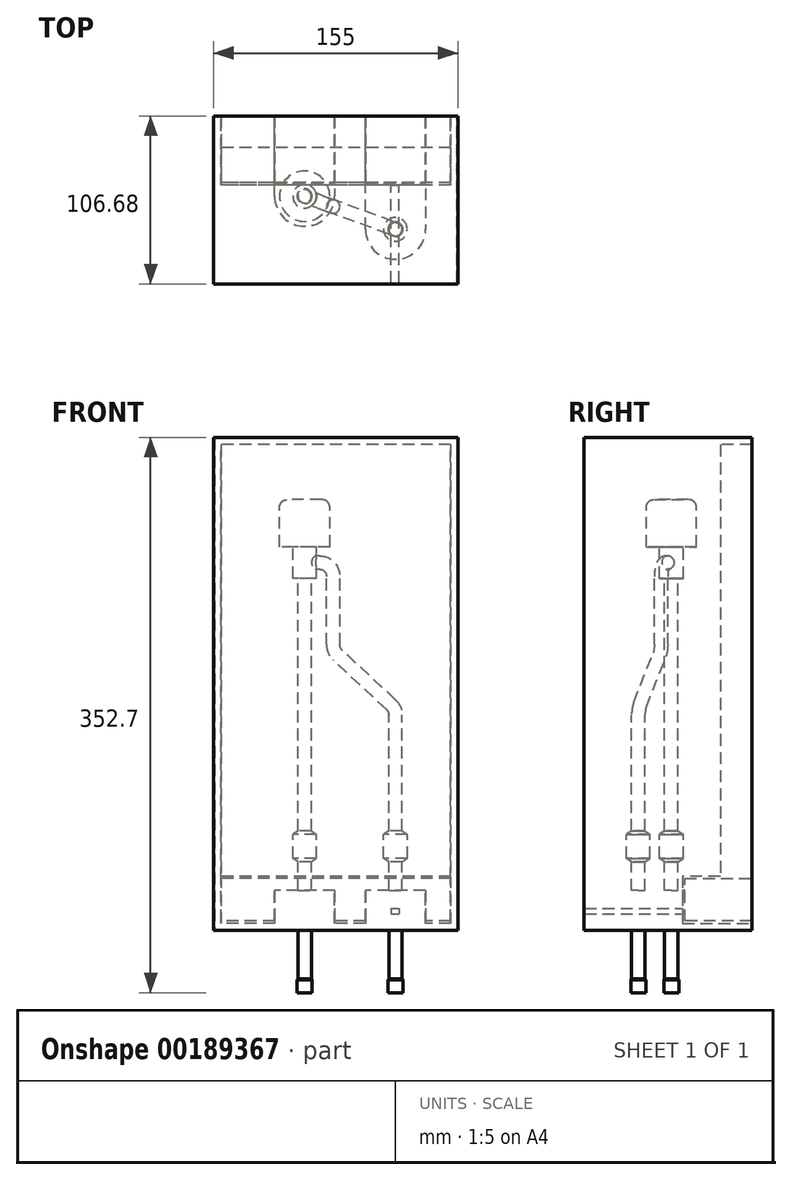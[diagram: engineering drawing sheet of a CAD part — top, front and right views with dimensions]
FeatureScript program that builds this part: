
annotation { "Feature Type Name" : "Feature", "Feature Type Description" : "" }
export const myFeature = defineFeature(function(context is Context, id is Id, definition is map)
    precondition{}
    {
        {
            var Q0;
            Q0=qCreatedBy(makeId("Right.planeOp"),FACE);
            var sketch = newSketch(context, id + "F0", { "sketchPlane" : qUnion([Q0])});
            skLineSegment(sketch, "E0", {"start": v(0, 302.68) * mm, "end": v(-20, 302.68) * mm});
            skLineSegment(sketch, "E1", {"start": v(-20, 302.68) * mm, "end": v(-20, 28.48) * mm});
            skLineSegment(sketch, "E2", {"start": v(-20, 28.48) * mm, "end": v(-44, 28.48) * mm});
            skLineSegment(sketch, "E3", {"start": v(-44, 28.48) * mm, "end": v(-44, -1.52) * mm});
            skLineSegment(sketch, "E4", {"start": v(-44, -1.52) * mm, "end": v(0, -1.52) * mm});
            skLineSegment(sketch, "E5", {"start": v(0, -1.52) * mm, "end": v(0, 0) * mm});
            skLineSegment(sketch, "E6", {"start": v(0, 0) * mm, "end": v(-42.48, 0) * mm});
            skLineSegment(sketch, "E7", {"start": v(-42.48, 0) * mm, "end": v(-42.48, 26.95) * mm});
            skLineSegment(sketch, "E8", {"start": v(-42.48, 26.95) * mm, "end": v(0, 26.95) * mm});
            skLineSegment(sketch, "E9", {"start": v(0, 26.95) * mm, "end": v(0, 302.68) * mm});
            skLineSegment(sketch, "E10", {"start": v(-42.48, 26.95) * mm, "end": v(-42.48, 28.48) * mm, "construction": true});
            skLineSegment(sketch, "E11", {"start": v(-42.48, 26.95) * mm, "end": v(-44, 26.95) * mm, "construction": true});
            skSolve(sketch);
        }
        {
            var Q0;
            Q0 = qSketchRegion(id + "F0", true);
            extrude(context, id + "F1", {"entities" : qUnion([Q0]), "endBound" : BoundingType.SYMMETRIC, "depth" : 146 * mm});
        }
        {
            var Q0;
            Q0=qCreatedBy(makeId("Front.planeOp"),FACE);
            cPlane(context, id + "F2", {"entities" : qUnion([Q0]), "cplaneType" : CPlaneType.OFFSET, "offset" : 51 * mm, "width" : 152.4 * mm, "height" : 152.4 * mm});
        }
        {
            var Q0;
            Q0=qCreatedBy(makeId("Front.planeOp"),FACE);
            cPlane(context, id + "F3", {"entities" : qUnion([Q0]), "cplaneType" : CPlaneType.OFFSET, "offset" : 72 * mm, "width" : 152.4 * mm, "height" : 152.4 * mm});
        }
        {
            var Q0;
            Q0=qCreatedBy(id+"F2.planeOp",FACE);
            var sketch = newSketch(context, id + "F4", { "sketchPlane" : qUnion([Q0])});
            skLineSegment(sketch, "E12", {"start": v(-19.78, 311.1) * mm, "end": v(-19.78, -128.37) * mm, "construction": true});
            skLineSegment(sketch, "E13", {"start": v(-19.78, 267.68) * mm, "end": v(-3.78, 267.68) * mm});
            skLineSegment(sketch, "E14", {"start": v(-3.78, 267.68) * mm, "end": v(-3.78, 237.68) * mm});
            skLineSegment(sketch, "E15", {"start": v(-3.78, 237.68) * mm, "end": v(-12.28, 237.68) * mm});
            skLineSegment(sketch, "E16", {"start": v(-12.28, 237.68) * mm, "end": v(-12.28, 217.68) * mm});
            skLineSegment(sketch, "E17", {"start": v(-12.28, 217.68) * mm, "end": v(-15.53, 217.68) * mm});
            skLineSegment(sketch, "E18", {"start": v(-15.53, 217.68) * mm, "end": v(-15.53, 57.25) * mm});
            skLineSegment(sketch, "E19", {"start": v(-15.53, 57.25) * mm, "end": v(-12.28, 54.92) * mm});
            skLineSegment(sketch, "E20", {"start": v(-12.28, 54.92) * mm, "end": v(-12.28, 39.92) * mm});
            skLineSegment(sketch, "E21", {"start": v(-12.28, 39.92) * mm, "end": v(-15.53, 37.58) * mm});
            skLineSegment(sketch, "E22", {"start": v(-15.53, 37.58) * mm, "end": v(-15.53, -36.66) * mm});
            skLineSegment(sketch, "E23", {"start": v(-15.53, -36.66) * mm, "end": v(-15.02, -37.52) * mm});
            skLineSegment(sketch, "E24", {"start": v(-15.02, -37.52) * mm, "end": v(-15.02, -45.52) * mm});
            skLineSegment(sketch, "E25", {"start": v(-15.02, -45.52) * mm, "end": v(-19.78, -45.52) * mm});
            skLineSegment(sketch, "E26", {"start": v(-19.78, 267.68) * mm, "end": v(-19.78, -45.52) * mm});
            skLineSegment(sketch, "E27", {"start": v(-12.28, 227.68) * mm, "end": v(-19.78, 227.68) * mm, "construction": true});
            skSolve(sketch);
        }
        {
            var Q0;
            Q0 = qSketchRegion(id + "F4", true);
            var Q1;
            Q1=sQuery(id+"F4.wireOp",EDGE,"E12");
            revolve(context, id + "F5", {"entities" : qUnion([Q0]), "axis" : qUnion([Q1]), "revolveType" : RevolveType.FULL});
        }
        {
            var Q0;
            Q0=makeQuery(id+"F5.opRevolve","SWEPT_EDGE",EDGE,{"disambiguationData":[OSD([sQuery(id+"F4.wireOp",EDGE,"E13"),sQuery(id+"F4.wireOp",EDGE,"E14")])]});
            fillet(context, id + "F6", {"entities" : qUnion([Q0]), "radius" : 5.08 * mm, "tangentPropagation" : true, "allowEdgeOverflow" : false});
        }
        {
            var Q0;
            Q0=qCreatedBy(id+"F3.planeOp",FACE);
            var sketch = newSketch(context, id + "F7", { "sketchPlane" : qUnion([Q0])});
            skLineSegment(sketch, "E28", {"start": v(37.92, 349.3) * mm, "end": v(37.92, -165.57) * mm, "construction": true});
            skLineSegment(sketch, "E29", {"start": v(37.92, -45.52) * mm, "end": v(42.68, -45.52) * mm});
            skLineSegment(sketch, "E30", {"start": v(42.68, -45.52) * mm, "end": v(42.68, -37.52) * mm});
            skLineSegment(sketch, "E31", {"start": v(42.68, -37.52) * mm, "end": v(42.17, -36.66) * mm});
            skLineSegment(sketch, "E32", {"start": v(42.17, -36.66) * mm, "end": v(42.17, 37.58) * mm});
            skLineSegment(sketch, "E33", {"start": v(42.17, 37.58) * mm, "end": v(45.42, 39.92) * mm});
            skLineSegment(sketch, "E34", {"start": v(45.42, 39.92) * mm, "end": v(45.42, 54.92) * mm});
            skLineSegment(sketch, "E35", {"start": v(45.42, 54.92) * mm, "end": v(42.17, 57.25) * mm});
            skLineSegment(sketch, "E36", {"start": v(42.17, 57.25) * mm, "end": v(42.17, 124.92) * mm});
            skLineSegment(sketch, "E37", {"start": v(42.17, 124.92) * mm, "end": v(37.92, 124.92) * mm});
            skLineSegment(sketch, "E38", {"start": v(37.92, 124.92) * mm, "end": v(37.92, -45.52) * mm});
            skSolve(sketch);
        }
        {
            var Q0;
            Q0 = qSketchRegion(id + "F7", true);
            var Q1;
            Q1=sQuery(id+"F7.wireOp",EDGE,"E28");
            revolve(context, id + "F8", {"entities" : qUnion([Q0]), "axis" : qUnion([Q1]), "revolveType" : RevolveType.FULL});
        }
        {
            var Q0;
            Q0=sQuery(id+"F7.wireOp",VERTEX,"E28.start");
            var Q1;
            Q1=sQuery(id+"F4.wireOp",VERTEX,"E27.end");
            var Q2;
            Q2=sQuery(id+"F7.wireOp",VERTEX,"E37.end");
            cPlane(context, id + "F9", {"entities" : qUnion([Q0, Q1, Q2]), "cplaneType" : CPlaneType.THREE_POINT, "offset" : 25.4 * mm, "width" : 152.4 * mm, "height" : 152.4 * mm});
        }
        {
            var Q0;
            Q0=qCreatedBy(id+"F9.planeOp",FACE);
            var sketch = newSketch(context, id + "F10", { "sketchPlane" : qUnion([Q0])});
            skLineSegment(sketch, "E39", {"start": v(-60.26, 124.92) * mm, "end": v(-60.26, 122.82) * mm, "construction": true});
            skLineSegment(sketch, "E40", {"start": v(-18.15, 175.57) * mm, "end": v(-18.15, 218.79) * mm});
            skLineSegment(sketch, "E41", {"start": v(-9.26, 227.68) * mm, "end": v(1.14, 227.68) * mm});
            skLineSegment(sketch, "E42", {"start": v(-60.26, 124.92) * mm, "end": v(-60.26, 130.75) * mm});
            skLineSegment(sketch, "E43", {"start": v(-57.21, 137.44) * mm, "end": v(-21.2, 168.87) * mm});
            skPoint(sketch, "E44.visualSharp", {"position": v(-18.15, 227.68) * mm});
            skArc(sketch, "E44.filletArc", {"start": v(-9.26, 227.68) * mm, "mid": v(-15.55, 225.07) * mm, "end": v(-18.15, 218.79) * mm});
            skPoint(sketch, "E45.visualSharp", {"position": v(-18.15, 171.53) * mm});
            skArc(sketch, "E45.filletArc", {"start": v(-21.2, 168.87) * mm, "mid": v(-18.95, 171.9) * mm, "end": v(-18.15, 175.57) * mm});
            skPoint(sketch, "E46.visualSharp", {"position": v(-60.26, 134.79) * mm});
            skArc(sketch, "E46.filletArc", {"start": v(-57.21, 137.44) * mm, "mid": v(-59.46, 134.42) * mm, "end": v(-60.26, 130.75) * mm});
            skSolve(sketch);
        }
        {
            var Q0;
            Q0=makeQuery(id+"F8.opRevolve","SWEPT_FACE",FACE,{"disambiguationData":[OSD([sQuery(id+"F7.wireOp",EDGE,"E37")])]});
            var Q1;
            Q1=sQuery(id+"F10.wireOp",EDGE,"E42");
            var Q2;
            Q2=sQuery(id+"F10.wireOp",EDGE,"E46.filletArc");
            var Q3;
            Q3=sQuery(id+"F10.wireOp",EDGE,"E43");
            var Q4;
            Q4=sQuery(id+"F10.wireOp",EDGE,"E45.filletArc");
            var Q5;
            Q5=sQuery(id+"F10.wireOp",EDGE,"E40");
            var Q6;
            Q6=sQuery(id+"F10.wireOp",EDGE,"E44.filletArc");
            var Q7;
            Q7=sQuery(id+"F10.wireOp",EDGE,"E41");
            sweep(context, id + "F11", {"operationType" : NewBodyOperationType.ADD, "profiles" : qUnion([Q0]), "path" : qUnion([Q1, Q2, Q3, Q4, Q5, Q6, Q7])});
        }
        {
            var Q0;
            Q0=qCreatedBy(makeId("Front.planeOp"),FACE);
            var sketch = newSketch(context, id + "F12", { "sketchPlane" : qUnion([Q0])});
            skLineSegment(sketch, "E47.bottom", {"start": v(-77, 306.68) * mm, "end": v(77, 306.68) * mm});
            skLineSegment(sketch, "E47.top", {"start": v(-77, -5.52) * mm, "end": v(77, -5.52) * mm});
            skLineSegment(sketch, "E47.left", {"start": v(-77, 306.68) * mm, "end": v(-77, -5.52) * mm});
            skLineSegment(sketch, "E47.right", {"start": v(77, 306.68) * mm, "end": v(77, -5.52) * mm});
            skLineSegment(sketch, "E48.bottom", {"start": v(-77.5, 307.18) * mm, "end": v(77.5, 307.18) * mm});
            skLineSegment(sketch, "E48.top", {"start": v(-77.5, -6.02) * mm, "end": v(77.5, -6.02) * mm});
            skLineSegment(sketch, "E48.left", {"start": v(-77.5, 307.18) * mm, "end": v(-77.5, -6.02) * mm});
            skLineSegment(sketch, "E48.right", {"start": v(77.5, 307.18) * mm, "end": v(77.5, -6.02) * mm});
            skLineSegment(sketch, "E49", {"start": v(-77, 306.68) * mm, "end": v(-77, 307.18) * mm, "construction": true});
            skLineSegment(sketch, "E50", {"start": v(-77, 306.68) * mm, "end": v(-77.5, 306.68) * mm, "construction": true});
            skLineSegment(sketch, "E51", {"start": v(77, -5.52) * mm, "end": v(77, -6.02) * mm, "construction": true});
            skLineSegment(sketch, "E52", {"start": v(77, -5.52) * mm, "end": v(77.5, -5.52) * mm, "construction": true});
            skLineSegment(sketch, "E53", {"start": v(-77, 302.68) * mm, "end": v(-73, 302.68) * mm, "construction": true});
            skLineSegment(sketch, "E54", {"start": v(-73, 306.68) * mm, "end": v(-73, 302.68) * mm, "construction": true});
            skLineSegment(sketch, "E55", {"start": v(77, -1.52) * mm, "end": v(73, -1.52) * mm, "construction": true});
            skLineSegment(sketch, "E56", {"start": v(73, -5.52) * mm, "end": v(73, -1.52) * mm, "construction": true});
            skSolve(sketch);
        }
        {
            var Q0;
            Q0 = qSketchRegion(id + "F12", true);
            var Q1;
            Q1=sQuery(id+"F12.wireOp",EDGE,"E48.bottom");
            var Q2;
            Q2=sQuery(id+"F12.wireOp",EDGE,"E48.right");
            var Q3;
            Q3=sQuery(id+"F12.wireOp",EDGE,"E48.top");
            var Q4;
            Q4=sQuery(id+"F12.wireOp",EDGE,"E48.left");
            extrude(context, id + "F13", {"entities" : qUnion([Q0]), "surfaceEntities" : qUnion([Q1, Q2, Q3, Q4]), "depth" : 106.68 * mm});
        }
        {
            var Q0;
            Q0=makeQuery(id+"F13.opExtrude","CAP_FACE",FACE,{"disambiguationData":[OSD([sQuery(id+"F12.wireOp",EDGE,"E47.bottom"),sQuery(id+"F12.wireOp",EDGE,"E47.top"),sQuery(id+"F12.wireOp",EDGE,"E47.left"),sQuery(id+"F12.wireOp",EDGE,"E47.right"),sQuery(id+"F12.wireOp",EDGE,"E48.bottom"),sQuery(id+"F12.wireOp",EDGE,"E48.top"),sQuery(id+"F12.wireOp",EDGE,"E48.left"),sQuery(id+"F12.wireOp",EDGE,"E48.right")])],"isStart":false});
            var sketch = newSketch(context, id + "F14", { "sketchPlane" : qUnion([Q0])});
            skLineSegment(sketch, "E57.0", {"start": v(-77.5, 307.18) * mm, "end": v(-77.5, -6.02) * mm});
            skLineSegment(sketch, "E57.1", {"start": v(-77.5, 307.18) * mm, "end": v(77.5, 307.18) * mm});
            skLineSegment(sketch, "E57.2", {"start": v(-77.5, -6.02) * mm, "end": v(77.5, -6.02) * mm});
            skLineSegment(sketch, "E57.3", {"start": v(77.5, 307.18) * mm, "end": v(77.5, -6.02) * mm});
            skSolve(sketch);
        }
        {
            var Q0;
            Q0 = qSketchRegion(id + "F14", true);
            var Q1;
            Q1 = qConstructionFilter(qBodyType(qCreatedBy(id + "F14" ,EDGE), BodyType.WIRE), ConstructionObject.NO);
            var Q2;
            Q2=makeQuery(id+"F13.opExtrude","SWEPT_FACE",FACE,{"disambiguationData":[OSD([sQuery(id+"F12.wireOp",EDGE,"E48.top")])]});
            extrude(context, id + "F15", {"entities" : qUnion([Q0]), "operationType" : NewBodyOperationType.ADD, "surfaceEntities" : qUnion([Q1]), "oppositeDirection" : true, "endBoundEntityFace" : qUnion([Q2]), "depth" : .5 * mm});
        }
        {
            var Q0;
            Q0=makeQuery(id+"F13.opExtrude","SWEPT_FACE",FACE,{"disambiguationData":[OSD([sQuery(id+"F12.wireOp",EDGE,"E48.top")])]});
            var sketch = newSketch(context, id + "F16", { "sketchPlane" : qUnion([Q0])});
            skCircle(sketch, "E58", {"center": v(-19.78, 51) * mm, "radius": 19.05 * mm});
            skCircle(sketch, "E59", {"center": v(37.92, 72) * mm, "radius": 19.05 * mm});
            skLineSegment(sketch, "E60", {"start": v(-38.83, 0) * mm, "end": v(-38.83, 51) * mm});
            skLineSegment(sketch, "E61", {"start": v(-38.83, 0) * mm, "end": v(-0.73, 0) * mm});
            skLineSegment(sketch, "E62", {"start": v(-0.73, 51) * mm, "end": v(-0.73, 0) * mm});
            skLineSegment(sketch, "E63", {"start": v(18.87, 0) * mm, "end": v(18.87, 72) * mm});
            skLineSegment(sketch, "E64", {"start": v(18.87, 0) * mm, "end": v(56.97, 0) * mm});
            skLineSegment(sketch, "E65", {"start": v(56.97, 72) * mm, "end": v(56.97, 0) * mm});
            skSolve(sketch);
        }
        {
            var Q0;
            Q0 = qSketchRegion(id + "F16", true);
            extrude(context, id + "F17", {"entities" : qUnion([Q0]), "operationType" : NewBodyOperationType.REMOVE, "oppositeDirection" : true, "depth" : 25.4 * mm});
        }
        {
            var Q0;
            Q0=makeQuery(id+"F1.opExtrude","SWEPT_FACE",FACE,{"disambiguationData":[OSD([sQuery(id+"F0.wireOp",EDGE,"E3")])]});
            var sketch = newSketch(context, id + "F18", { "sketchPlane" : qUnion([Q0])});
            skLineSegment(sketch, "E66.bottom", {"start": v(35.14, 7.89) * mm, "end": v(40.28, 7.89) * mm});
            skLineSegment(sketch, "E66.top", {"start": v(35.14, 4.52) * mm, "end": v(40.28, 4.52) * mm});
            skLineSegment(sketch, "E66.left", {"start": v(35.14, 7.89) * mm, "end": v(35.14, 4.52) * mm});
            skLineSegment(sketch, "E66.right", {"start": v(40.28, 7.89) * mm, "end": v(40.28, 4.52) * mm});
            skSolve(sketch);
        }
        {
            var Q0;
            Q0 = qSketchRegion(id + "F18", true);
            var Q1;
            Q1=makeQuery(id+"F15.opExtrude","CAP_FACE",FACE,{"disambiguationData":[OSD([sQuery(id+"F14.wireOp",EDGE,"E57.0"),sQuery(id+"F14.wireOp",EDGE,"E57.1"),sQuery(id+"F14.wireOp",EDGE,"E57.2"),sQuery(id+"F14.wireOp",EDGE,"E57.3")])],"isStart":false});
            extrude(context, id + "F19", {"entities" : qUnion([Q0]), "operationType" : NewBodyOperationType.ADD, "endBound" : BoundingType.UP_TO_SURFACE, "endBoundEntityFace" : qUnion([Q1]), "depth" : 25.4 * mm});
        }
    });
